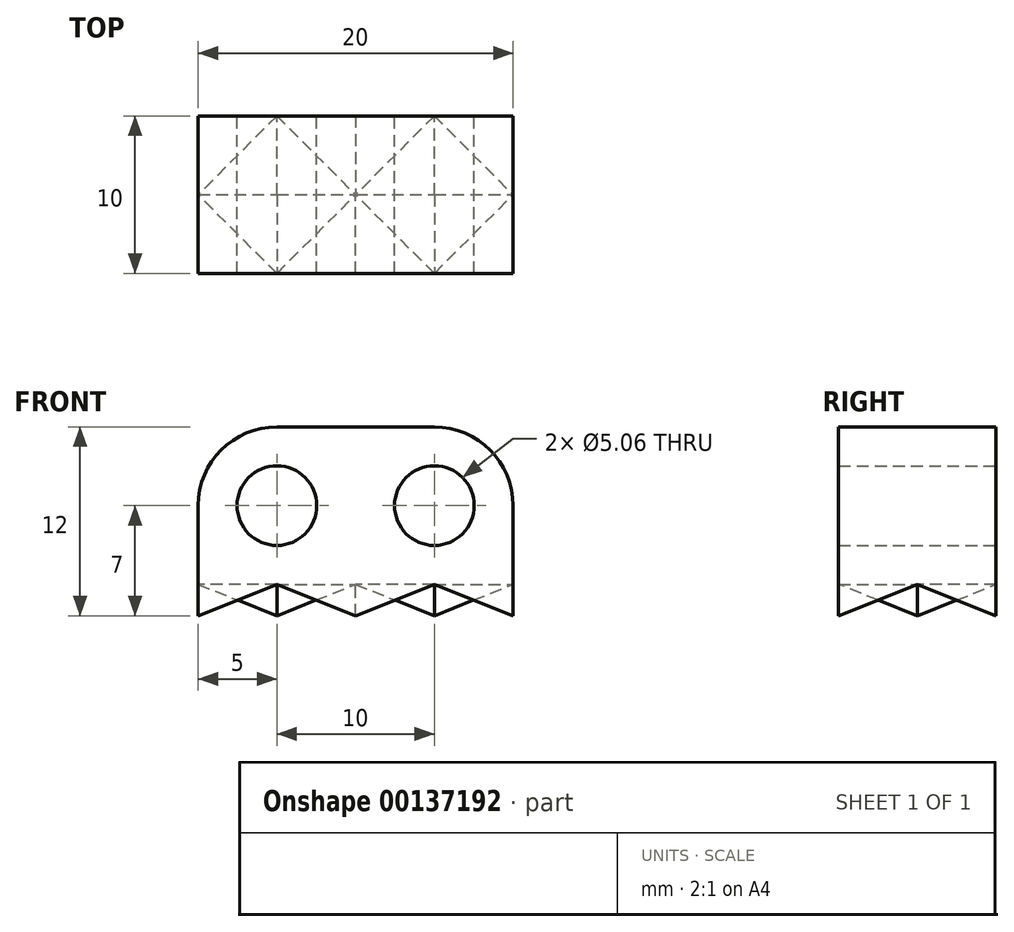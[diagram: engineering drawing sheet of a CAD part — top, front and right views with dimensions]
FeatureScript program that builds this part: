
annotation { "Feature Type Name" : "Feature", "Feature Type Description" : "" }
export const myFeature = defineFeature(function(context is Context, id is Id, definition is map)
    precondition{}
    {
        {
            var Q0;
            Q0=qCreatedBy(makeId("Front.planeOp"),FACE);
            var sketch = newSketch(context, id + "F0", { "sketchPlane" : qUnion([Q0])});
            skLineSegment(sketch, "E0.bottom", {"start": v(-5, 5) * mm, "end": v(5, 5) * mm});
            skLineSegment(sketch, "E0.top", {"start": v(-10, -5) * mm, "end": v(10, -5) * mm});
            skLineSegment(sketch, "E0.left", {"start": v(-10, 0) * mm, "end": v(-10, -5) * mm});
            skLineSegment(sketch, "E0.right", {"start": v(10, 0) * mm, "end": v(10, -5) * mm});
            skPoint(sketch, "E0.middle", {"position": v(0, 0) * mm});
            skCircle(sketch, "E1", {"center": v(-5, 0) * mm, "radius": 2.53 * mm});
            skCircle(sketch, "E2", {"center": v(5, 0) * mm, "radius": 2.53 * mm});
            skPoint(sketch, "E3.visualSharp", {"position": v(-10, 5) * mm});
            skArc(sketch, "E3.filletArc", {"start": v(-5, 5) * mm, "mid": v(-8.54, 3.54) * mm, "end": v(-10, 0) * mm});
            skPoint(sketch, "E4.visualSharp", {"position": v(10, 5) * mm});
            skArc(sketch, "E4.filletArc", {"start": v(10, 0) * mm, "mid": v(8.54, 3.54) * mm, "end": v(5, 5) * mm});
            skSolve(sketch);
        }
        {
            var Q0;
            Q0=makeQuery(id+"F0.imprint","IMPRINT",FACE,{"disambiguationData":[TD([[makeQuery(id+"F0.imprint","IMPRINT",EDGE,{"derivedFrom":sQuery(id+"F0.wireOp",EDGE,"E0.bottom")}),-1.0]])]});
            extrude(context, id + "F1", {"entities" : qUnion([Q0]), "depth" : 10 * mm});
        }
        {
            var Q0;
            Q0=makeQuery(id+"F1.opExtrude","CAP_FACE",FACE,{"disambiguationData":[OSD([sQuery(id+"F0.wireOp",EDGE,"E0.bottom"),sQuery(id+"F0.wireOp",EDGE,"E0.top"),sQuery(id+"F0.wireOp",EDGE,"E0.left"),sQuery(id+"F0.wireOp",EDGE,"E0.right"),sQuery(id+"F0.wireOp",EDGE,"E1"),sQuery(id+"F0.wireOp",EDGE,"E2"),sQuery(id+"F0.wireOp",EDGE,"E3.filletArc"),sQuery(id+"F0.wireOp",EDGE,"E4.filletArc")])],"isStart":false});
            var sketch = newSketch(context, id + "F2", { "sketchPlane" : qUnion([Q0])});
            skLineSegment(sketch, "E5", {"start": v(-10, -5) * mm, "end": v(-10, -7) * mm});
            skLineSegment(sketch, "E6", {"start": v(-10, -7) * mm, "end": v(-5, -5) * mm});
            skLineSegment(sketch, "E7", {"start": v(-5, -5) * mm, "end": v(0, -7) * mm});
            skLineSegment(sketch, "E8", {"start": v(0, -7) * mm, "end": v(5, -5) * mm});
            skLineSegment(sketch, "E9", {"start": v(5, -5) * mm, "end": v(10, -7) * mm});
            skLineSegment(sketch, "E10", {"start": v(10, -7) * mm, "end": v(10, -5) * mm});
            skLineSegment(sketch, "E11", {"start": v(10, -5) * mm, "end": v(-10, -5) * mm});
            skSolve(sketch);
        }
        {
            var Q0;
            Q0=makeQuery(id+"F1.opExtrude","CAP_FACE",FACE,{"disambiguationData":[OSD([sQuery(id+"F0.wireOp",EDGE,"E0.bottom"),sQuery(id+"F0.wireOp",EDGE,"E0.top"),sQuery(id+"F0.wireOp",EDGE,"E0.left"),sQuery(id+"F0.wireOp",EDGE,"E0.right"),sQuery(id+"F0.wireOp",EDGE,"E1"),sQuery(id+"F0.wireOp",EDGE,"E2"),sQuery(id+"F0.wireOp",EDGE,"E3.filletArc"),sQuery(id+"F0.wireOp",EDGE,"E4.filletArc")])],"isStart":true});
            var sketch = newSketch(context, id + "F3", { "sketchPlane" : qUnion([Q0])});
            skLineSegment(sketch, "E12.0", {"start": v(10, -7) * mm, "end": v(5, -5) * mm});
            skLineSegment(sketch, "E13.0.3", {"start": v(-10, -5) * mm, "end": v(10, -5) * mm});
            skLineSegment(sketch, "E14.0", {"start": v(5, -5) * mm, "end": v(0, -7) * mm});
            skLineSegment(sketch, "E14.1", {"start": v(0, -7) * mm, "end": v(-5, -5) * mm});
            skLineSegment(sketch, "E15.0", {"start": v(-5, -5) * mm, "end": v(-10, -7) * mm});
            skLineSegment(sketch, "E15.1", {"start": v(-10, -7) * mm, "end": v(-10, -5) * mm});
            skLineSegment(sketch, "E16.0", {"start": v(10, -5) * mm, "end": v(10, -7) * mm});
            skSolve(sketch);
        }
        {
            var Q0;
            Q0=makeQuery(id+"F3.imprint","IMPRINT",FACE,{"disambiguationData":[TD([[makeQuery(id+"F3.imprint","IMPRINT",EDGE,{"derivedFrom":makeQuery(id+"F1.opExtrude","CAP_EDGE",EDGE,{"disambiguationData":[OSD([sQuery(id+"F0.wireOp",EDGE,"E0.bottom")])],"isStart":true})}),1.0]])]});
            cPlane(context, id + "F4", {"entities" : qUnion([Q0]), "cplaneType" : CPlaneType.OFFSET, "offset" : 5 * mm, "oppositeDirection" : true, "width" : 150 * mm, "height" : 150 * mm});
        }
        {
            var Q0;
            Q0=qCreatedBy(id+"F4.planeOp",FACE);
            var sketch = newSketch(context, id + "F5", { "sketchPlane" : qUnion([Q0])});
            skPoint(sketch, "E17.0", {"position": v(10, -5) * mm});
            skPoint(sketch, "E18.0", {"position": v(5, -5) * mm});
            skPoint(sketch, "E19.0", {"position": v(0, -7) * mm});
            skPoint(sketch, "E20.0", {"position": v(-5, -5) * mm});
            skPoint(sketch, "E21.0", {"position": v(-10, -5) * mm});
            skPoint(sketch, "E22.0", {"position": v(-10, -7) * mm});
            skPoint(sketch, "E23.0", {"position": v(10, -7) * mm});
            skLineSegment(sketch, "E24", {"start": v(10, -5) * mm, "end": v(5, -7) * mm});
            skLineSegment(sketch, "E25", {"start": v(5, -7) * mm, "end": v(0, -5) * mm});
            skLineSegment(sketch, "E26", {"start": v(0, -5) * mm, "end": v(-5, -7) * mm});
            skLineSegment(sketch, "E27", {"start": v(-5, -7) * mm, "end": v(-10, -5) * mm});
            skLineSegment(sketch, "E28", {"start": v(10, -5) * mm, "end": v(-10, -5) * mm});
            skSolve(sketch);
        }
        {
            var Q1;
            {var subQ0=sQuery(id+"F3.wireOp",EDGE,"E14.0");Q1=makeQuery(id+"F3.imprint","IMPRINT",FACE,{"disambiguationData":[TD([[makeQuery(id+"F3.imprint","IMPRINT",EDGE,{"derivedFrom":subQ0}),-1.0]])]});}
            var Q2;
            Q2=sQuery(id+"F5.wireOp",VERTEX,"E26.start");
            loft(context, id + "F6", {"operationType" : NewBodyOperationType.ADD, "sheetProfilesArray" : [{ "sheetProfileEntities" : qUnion([Q1]) }, { "sheetProfileEntities" : qUnion([Q2]) }]});
        }
        {
            var Q1;
            {var subQ0=sQuery(id+"F3.wireOp",EDGE,"E12.0");Q1=makeQuery(id+"F3.imprint","IMPRINT",FACE,{"disambiguationData":[TD([[makeQuery(id+"F3.imprint","IMPRINT",EDGE,{"derivedFrom":subQ0}),-1.0]])]});}
            var Q2;
            Q2=sQuery(id+"F5.wireOp",VERTEX,"E17.0");
            loft(context, id + "F7", {"operationType" : NewBodyOperationType.ADD, "sheetProfilesArray" : [{ "sheetProfileEntities" : qUnion([Q1]) }, { "sheetProfileEntities" : qUnion([Q2]) }]});
        }
        {
            var Q1;
            {var subQ0=sQuery(id+"F5.wireOp",EDGE,"E24");Q1=makeQuery(id+"F5.imprint","IMPRINT",FACE,{"disambiguationData":[TD([[makeQuery(id+"F5.imprint","IMPRINT",EDGE,{"derivedFrom":subQ0}),-1.0]])]});}
            var Q2;
            Q2=sQuery(id+"F3.wireOp",VERTEX,"E14.0.start");
            loft(context, id + "F8", {"operationType" : NewBodyOperationType.ADD, "sheetProfilesArray" : [{ "sheetProfileEntities" : qUnion([Q1]) }, { "sheetProfileEntities" : qUnion([Q2]) }]});
        }
        {
            var Q1;
            {var subQ0=sQuery(id+"F3.wireOp",EDGE,"E15.0");Q1=makeQuery(id+"F3.imprint","IMPRINT",FACE,{"disambiguationData":[TD([[makeQuery(id+"F3.imprint","IMPRINT",EDGE,{"derivedFrom":subQ0}),-1.0]])]});}
            var Q2;
            Q2=sQuery(id+"F5.wireOp",VERTEX,"E21.0");
            loft(context, id + "F9", {"operationType" : NewBodyOperationType.ADD, "sheetProfilesArray" : [{ "sheetProfileEntities" : qUnion([Q1]) }, { "sheetProfileEntities" : qUnion([Q2]) }]});
        }
        {
            var Q1;
            {var subQ0=sQuery(id+"F5.wireOp",EDGE,"E26");Q1=makeQuery(id+"F5.imprint","IMPRINT",FACE,{"disambiguationData":[TD([[makeQuery(id+"F5.imprint","IMPRINT",EDGE,{"derivedFrom":subQ0}),-1.0]])]});}
            var Q2;
            Q2=sQuery(id+"F3.wireOp",VERTEX,"E15.0.start");
            loft(context, id + "F10", {"operationType" : NewBodyOperationType.ADD, "sheetProfilesArray" : [{ "sheetProfileEntities" : qUnion([Q1]) }, { "sheetProfileEntities" : qUnion([Q2]) }]});
        }
        {
            var Q1;
            {var subQ0=sQuery(id+"F2.wireOp",EDGE,"E5");Q1=makeQuery(id+"F2.imprint","IMPRINT",FACE,{"disambiguationData":[TD([[makeQuery(id+"F2.imprint","IMPRINT",EDGE,{"derivedFrom":subQ0}),1.0]])]});}
            var Q2;
            Q2=sQuery(id+"F5.wireOp",VERTEX,"E17.0");
            loft(context, id + "F11", {"operationType" : NewBodyOperationType.ADD, "sheetProfilesArray" : [{ "sheetProfileEntities" : qUnion([Q1]) }, { "sheetProfileEntities" : qUnion([Q2]) }]});
        }
        {
            var Q1;
            {var subQ0=sQuery(id+"F2.wireOp",EDGE,"E9");Q1=makeQuery(id+"F2.imprint","IMPRINT",FACE,{"disambiguationData":[TD([[makeQuery(id+"F2.imprint","IMPRINT",EDGE,{"derivedFrom":subQ0}),1.0]])]});}
            var Q2;
            Q2=sQuery(id+"F5.wireOp",VERTEX,"E21.0");
            loft(context, id + "F12", {"operationType" : NewBodyOperationType.ADD, "sheetProfilesArray" : [{ "sheetProfileEntities" : qUnion([Q1]) }, { "sheetProfileEntities" : qUnion([Q2]) }]});
        }
        {
            var Q1;
            {var subQ0=sQuery(id+"F2.wireOp",EDGE,"E7");Q1=makeQuery(id+"F2.imprint","IMPRINT",FACE,{"disambiguationData":[TD([[makeQuery(id+"F2.imprint","IMPRINT",EDGE,{"derivedFrom":subQ0}),1.0]])]});}
            var Q2;
            Q2=sQuery(id+"F5.wireOp",VERTEX,"E26.start");
            loft(context, id + "F13", {"operationType" : NewBodyOperationType.ADD, "sheetProfilesArray" : [{ "sheetProfileEntities" : qUnion([Q1]) }, { "sheetProfileEntities" : qUnion([Q2]) }]});
        }
        {
            var Q1;
            {var subQ0=sQuery(id+"F5.wireOp",EDGE,"E24");Q1=makeQuery(id+"F5.imprint","IMPRINT",FACE,{"disambiguationData":[TD([[makeQuery(id+"F5.imprint","IMPRINT",EDGE,{"derivedFrom":subQ0}),-1.0]])]});}
            var Q2;
            Q2=sQuery(id+"F2.wireOp",VERTEX,"E7.start");
            loft(context, id + "F14", {"operationType" : NewBodyOperationType.ADD, "sheetProfilesArray" : [{ "sheetProfileEntities" : qUnion([Q1]) }, { "sheetProfileEntities" : qUnion([Q2]) }]});
        }
        {
            var Q1;
            {var subQ0=sQuery(id+"F5.wireOp",EDGE,"E26");Q1=makeQuery(id+"F5.imprint","IMPRINT",FACE,{"disambiguationData":[TD([[makeQuery(id+"F5.imprint","IMPRINT",EDGE,{"derivedFrom":subQ0}),-1.0]])]});}
            var Q2;
            Q2=sQuery(id+"F2.wireOp",VERTEX,"E9.start");
            loft(context, id + "F15", {"operationType" : NewBodyOperationType.ADD, "sheetProfilesArray" : [{ "sheetProfileEntities" : qUnion([Q1]) }, { "sheetProfileEntities" : qUnion([Q2]) }]});
        }
    });
